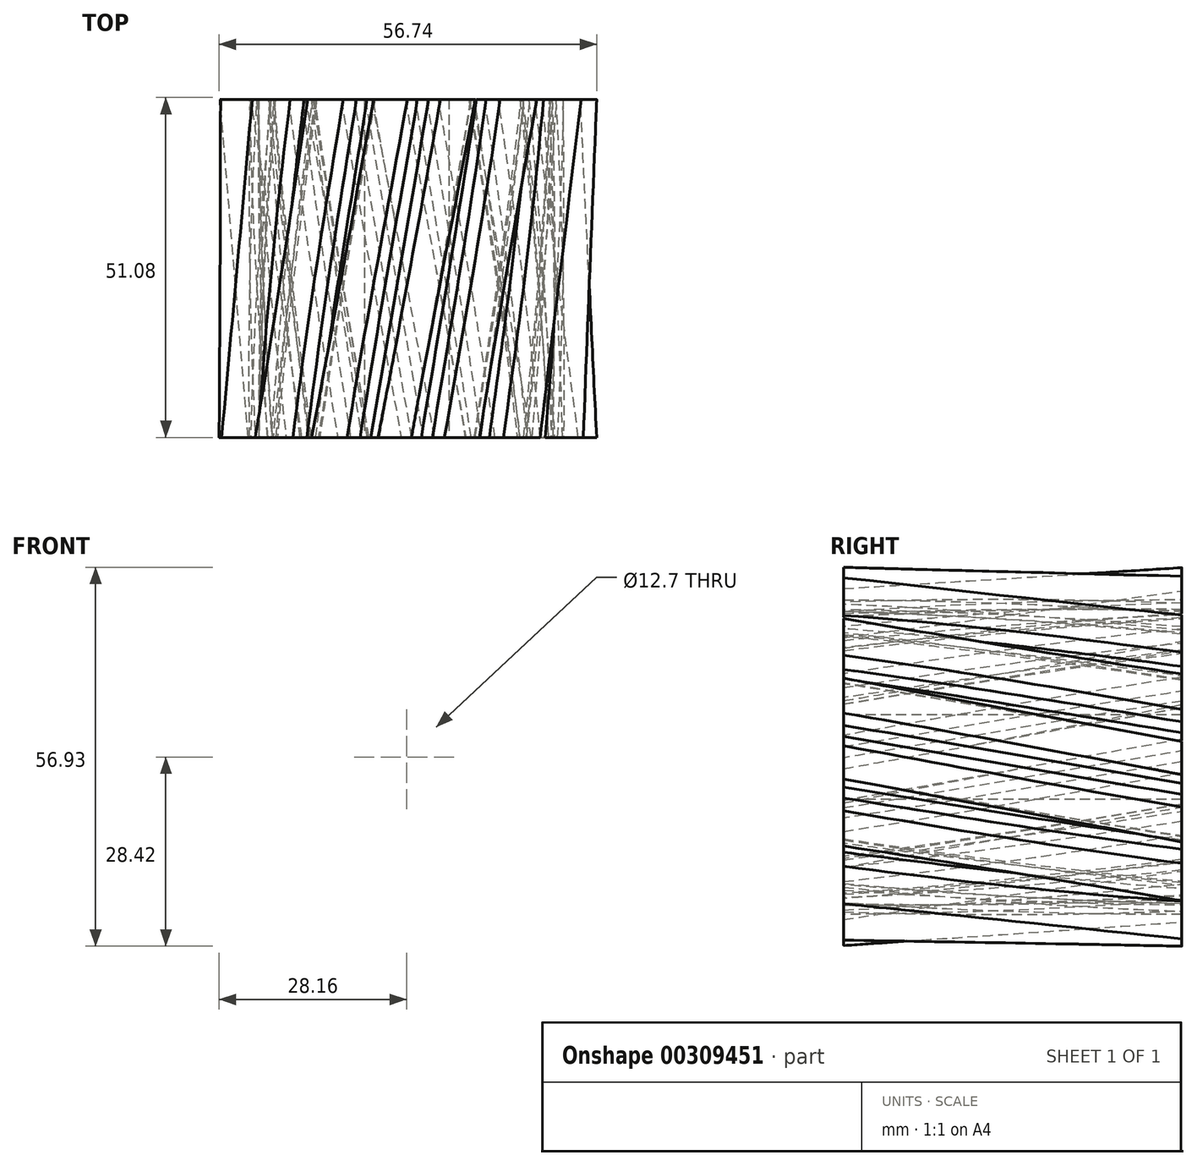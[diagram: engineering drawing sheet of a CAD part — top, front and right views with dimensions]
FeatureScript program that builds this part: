
annotation { "Feature Type Name" : "Feature", "Feature Type Description" : "" }
export const myFeature = defineFeature(function(context is Context, id is Id, definition is map)
    precondition{}
    {
        {
            var Q0;
            Q0=qCreatedBy(makeId("Front.planeOp"),FACE);
            var sketch = newSketch(context, id + "F0", { "sketchPlane" : qUnion([Q0])});
            skCircle(sketch, "E0", {"center": v(0, 0) * mm, "radius": 22.23 * mm});
            skArc(sketch, "E1.trimOffspring", {"start": v(-0.11, 25.67) * mm, "mid": v(-1.04, 27.17) * mm, "end": v(-2.34, 28.36) * mm});
            skLineSegment(sketch, "E2", {"start": v(0.02, 25.15) * mm, "end": v(0.23, 22.22) * mm});
            skLineSegment(sketch, "E3", {"start": v(-2.68, 28.45) * mm, "end": v(-2.8, 28.44) * mm});
            skLineSegment(sketch, "E4.MirrorCS", {"start": v(-2.93, 28.43) * mm, "end": v(-2.8, 28.44) * mm});
            skArc(sketch, "E5.MirrorCS", {"start": v(-4.9, 25.2) * mm, "mid": v(-4.28, 26.86) * mm, "end": v(-3.23, 28.28) * mm});
            skLineSegment(sketch, "E6.MirrorCS", {"start": v(-4.92, 24.66) * mm, "end": v(-4.56, 21.75) * mm});
            skPoint(sketch, "E7.visualSharp", {"position": v(0, 25.4) * mm});
            skArc(sketch, "E7.filletArc", {"start": v(0.02, 25.15) * mm, "mid": v(-0.02, 25.41) * mm, "end": v(-0.11, 25.67) * mm});
            skPoint(sketch, "E8.visualSharp", {"position": v(-4.96, 24.91) * mm});
            skArc(sketch, "E8.filletArc", {"start": v(-4.9, 25.2) * mm, "mid": v(-4.93, 24.93) * mm, "end": v(-4.92, 24.66) * mm});
            skPoint(sketch, "E9.visualSharp", {"position": v(-2.5, 28.47) * mm});
            skArc(sketch, "E9.filletArc", {"start": v(-2.34, 28.36) * mm, "mid": v(-2.5, 28.44) * mm, "end": v(-2.68, 28.45) * mm});
            skPoint(sketch, "E10.visualSharp", {"position": v(-3.1, 28.4) * mm});
            skArc(sketch, "E10.filletArc", {"start": v(-2.93, 28.43) * mm, "mid": v(-3.1, 28.38) * mm, "end": v(-3.23, 28.28) * mm});
            skSolve(sketch);
        }
        {
            var Q0;
            Q0=qCreatedBy(makeId("Front.planeOp"),FACE);
            cPlane(context, id + "F1", {"entities" : qUnion([Q0]), "cplaneType" : CPlaneType.OFFSET, "offset" : 50.8 * mm, "width" : 152.4 * mm, "height" : 152.4 * mm});
        }
        {
            var Q0;
            Q0=qCreatedBy(id+"F1.planeOp",FACE);
            var sketch = newSketch(context, id + "F2", { "sketchPlane" : qUnion([Q0])});
            skCircle(sketch, "E11.0", {"center": v(0, 0) * mm, "radius": 22.23 * mm});
            skArc(sketch, "E12.0.0", {"start": v(-3.23, 28.28) * mm, "mid": v(-4.28, 26.86) * mm, "end": v(-4.9, 25.2) * mm});
            skArc(sketch, "E12.0.1", {"start": v(-4.9, 25.2) * mm, "mid": v(-4.93, 24.93) * mm, "end": v(-4.92, 24.66) * mm});
            skLineSegment(sketch, "E12.0.2", {"start": v(-4.92, 24.66) * mm, "end": v(-4.56, 21.75) * mm});
            skArc(sketch, "E12.0.3", {"start": v(-4.56, 21.75) * mm, "mid": v(-2.18, 22.12) * mm, "end": v(0.23, 22.22) * mm});
            skLineSegment(sketch, "E12.0.4", {"start": v(0.23, 22.22) * mm, "end": v(0.02, 25.15) * mm});
            skArc(sketch, "E12.0.5", {"start": v(0.02, 25.15) * mm, "mid": v(-0.02, 25.41) * mm, "end": v(-0.11, 25.67) * mm});
            skArc(sketch, "E12.0.6", {"start": v(-0.11, 25.67) * mm, "mid": v(-1.04, 27.17) * mm, "end": v(-2.34, 28.36) * mm});
            skArc(sketch, "E12.0.7", {"start": v(-2.34, 28.36) * mm, "mid": v(-2.5, 28.44) * mm, "end": v(-2.68, 28.45) * mm});
            skLineSegment(sketch, "E12.0.8", {"start": v(-2.68, 28.45) * mm, "end": v(-2.8, 28.44) * mm});
            skLineSegment(sketch, "E12.0.9", {"start": v(-2.8, 28.44) * mm, "end": v(-2.93, 28.43) * mm});
            skArc(sketch, "E12.0.10", {"start": v(-2.93, 28.43) * mm, "mid": v(-3.1, 28.38) * mm, "end": v(-3.23, 28.28) * mm});
            skLineSegment(sketch, "E13.1.0", {"start": v(-13.99, 20.9) * mm, "end": v(-12.54, 18.35) * mm});
            skLineSegment(sketch, "E13.1.1", {"start": v(-13.47, 25.2) * mm, "end": v(-13.58, 25.14) * mm});
            skLineSegment(sketch, "E13.1.2", {"start": v(-13.36, 25.26) * mm, "end": v(-13.47, 25.2) * mm});
            skArc(sketch, "E13.1.3", {"start": v(-13.58, 25.14) * mm, "mid": v(-13.72, 25.03) * mm, "end": v(-13.8, 24.89) * mm});
            skArc(sketch, "E13.1.4", {"start": v(-13.02, 25.3) * mm, "mid": v(-13.2, 25.31) * mm, "end": v(-13.36, 25.26) * mm});
            skArc(sketch, "E13.1.5", {"start": v(-9.93, 23.68) * mm, "mid": v(-11.36, 24.7) * mm, "end": v(-13.02, 25.3) * mm});
            skArc(sketch, "E13.1.6", {"start": v(-13.8, 24.89) * mm, "mid": v(-14.23, 23.17) * mm, "end": v(-14.17, 21.4) * mm});
            skArc(sketch, "E13.1.7", {"start": v(-14.17, 21.4) * mm, "mid": v(-14.1, 21.15) * mm, "end": v(-13.99, 20.9) * mm});
            skArc(sketch, "E13.1.8", {"start": v(-9.6, 23.24) * mm, "mid": v(-9.75, 23.47) * mm, "end": v(-9.93, 23.68) * mm});
            skLineSegment(sketch, "E13.1.9", {"start": v(-8.3, 20.62) * mm, "end": v(-9.6, 23.24) * mm});
            skLineSegment(sketch, "E13.2.0", {"start": v(-20.92, 13.95) * mm, "end": v(-18.6, 12.15) * mm});
            skLineSegment(sketch, "E13.2.1", {"start": v(-22.1, 18.13) * mm, "end": v(-22.17, 18.03) * mm});
            skLineSegment(sketch, "E13.2.2", {"start": v(-22, 18.23) * mm, "end": v(-22.1, 18.13) * mm});
            skArc(sketch, "E13.2.3", {"start": v(-22.17, 18.03) * mm, "mid": v(-22.25, 17.88) * mm, "end": v(-22.28, 17.7) * mm});
            skArc(sketch, "E13.2.4", {"start": v(-21.71, 18.4) * mm, "mid": v(-21.88, 18.34) * mm, "end": v(-22, 18.23) * mm});
            skArc(sketch, "E13.2.5", {"start": v(-18.23, 18.07) * mm, "mid": v(-19.95, 18.48) * mm, "end": v(-21.71, 18.4) * mm});
            skArc(sketch, "E13.2.6", {"start": v(-22.28, 17.7) * mm, "mid": v(-22.02, 15.96) * mm, "end": v(-21.28, 14.36) * mm});
            skArc(sketch, "E13.2.7", {"start": v(-21.28, 14.36) * mm, "mid": v(-21.12, 14.14) * mm, "end": v(-20.92, 13.95) * mm});
            skArc(sketch, "E13.2.8", {"start": v(-17.77, 17.8) * mm, "mid": v(-17.99, 17.95) * mm, "end": v(-18.23, 18.07) * mm});
            skLineSegment(sketch, "E13.2.9", {"start": v(-15.55, 15.88) * mm, "end": v(-17.77, 17.8) * mm});
            skLineSegment(sketch, "E13.3.0", {"start": v(-24.67, 4.89) * mm, "end": v(-21.84, 4.1) * mm});
            skLineSegment(sketch, "E13.3.1", {"start": v(-27.35, 8.3) * mm, "end": v(-27.38, 8.17) * mm});
            skLineSegment(sketch, "E13.3.2", {"start": v(-27.3, 8.42) * mm, "end": v(-27.35, 8.3) * mm});
            skArc(sketch, "E13.3.3", {"start": v(-27.38, 8.17) * mm, "mid": v(-27.4, 8) * mm, "end": v(-27.36, 7.83) * mm});
            skArc(sketch, "E13.3.4", {"start": v(-27.1, 8.69) * mm, "mid": v(-27.23, 8.57) * mm, "end": v(-27.3, 8.42) * mm});
            skArc(sketch, "E13.3.5", {"start": v(-23.76, 9.72) * mm, "mid": v(-25.5, 9.44) * mm, "end": v(-27.1, 8.69) * mm});
            skArc(sketch, "E13.3.6", {"start": v(-27.36, 7.83) * mm, "mid": v(-26.45, 6.32) * mm, "end": v(-25.16, 5.12) * mm});
            skArc(sketch, "E13.3.7", {"start": v(-25.16, 5.12) * mm, "mid": v(-24.92, 4.98) * mm, "end": v(-24.67, 4.89) * mm});
            skArc(sketch, "E13.3.8", {"start": v(-23.22, 9.64) * mm, "mid": v(-23.49, 9.7) * mm, "end": v(-23.76, 9.72) * mm});
            skLineSegment(sketch, "E13.3.9", {"start": v(-20.44, 8.72) * mm, "end": v(-23.22, 9.64) * mm});
            skLineSegment(sketch, "E13.4.0", {"start": v(-24.66, -4.92) * mm, "end": v(-21.75, -4.56) * mm});
            skLineSegment(sketch, "E13.4.1", {"start": v(-28.44, -2.8) * mm, "end": v(-28.43, -2.93) * mm});
            skLineSegment(sketch, "E13.4.2", {"start": v(-28.45, -2.68) * mm, "end": v(-28.44, -2.8) * mm});
            skArc(sketch, "E13.4.3", {"start": v(-28.43, -2.93) * mm, "mid": v(-28.38, -3.1) * mm, "end": v(-28.28, -3.23) * mm});
            skArc(sketch, "E13.4.4", {"start": v(-28.36, -2.34) * mm, "mid": v(-28.44, -2.5) * mm, "end": v(-28.45, -2.68) * mm});
            skArc(sketch, "E13.4.5", {"start": v(-25.67, -0.11) * mm, "mid": v(-27.17, -1.04) * mm, "end": v(-28.36, -2.34) * mm});
            skArc(sketch, "E13.4.6", {"start": v(-28.28, -3.23) * mm, "mid": v(-26.86, -4.28) * mm, "end": v(-25.2, -4.9) * mm});
            skArc(sketch, "E13.4.7", {"start": v(-25.2, -4.9) * mm, "mid": v(-24.93, -4.93) * mm, "end": v(-24.66, -4.92) * mm});
            skArc(sketch, "E13.4.8", {"start": v(-25.15, 0.02) * mm, "mid": v(-25.41, -0.02) * mm, "end": v(-25.67, -0.11) * mm});
            skLineSegment(sketch, "E13.4.9", {"start": v(-22.22, 0.23) * mm, "end": v(-25.15, 0.02) * mm});
            skLineSegment(sketch, "E13.5.0", {"start": v(-20.9, -13.99) * mm, "end": v(-18.35, -12.54) * mm});
            skLineSegment(sketch, "E13.5.1", {"start": v(-25.2, -13.47) * mm, "end": v(-25.14, -13.58) * mm});
            skLineSegment(sketch, "E13.5.2", {"start": v(-25.26, -13.36) * mm, "end": v(-25.2, -13.47) * mm});
            skArc(sketch, "E13.5.3", {"start": v(-25.14, -13.58) * mm, "mid": v(-25.03, -13.72) * mm, "end": v(-24.89, -13.8) * mm});
            skArc(sketch, "E13.5.4", {"start": v(-25.3, -13.02) * mm, "mid": v(-25.31, -13.2) * mm, "end": v(-25.26, -13.36) * mm});
            skArc(sketch, "E13.5.5", {"start": v(-23.68, -9.93) * mm, "mid": v(-24.7, -11.36) * mm, "end": v(-25.3, -13.02) * mm});
            skArc(sketch, "E13.5.6", {"start": v(-24.89, -13.8) * mm, "mid": v(-23.17, -14.23) * mm, "end": v(-21.4, -14.17) * mm});
            skArc(sketch, "E13.5.7", {"start": v(-21.4, -14.17) * mm, "mid": v(-21.15, -14.1) * mm, "end": v(-20.9, -13.99) * mm});
            skArc(sketch, "E13.5.8", {"start": v(-23.24, -9.6) * mm, "mid": v(-23.47, -9.75) * mm, "end": v(-23.68, -9.93) * mm});
            skLineSegment(sketch, "E13.5.9", {"start": v(-20.62, -8.3) * mm, "end": v(-23.24, -9.6) * mm});
            skLineSegment(sketch, "E13.6.0", {"start": v(-13.95, -20.92) * mm, "end": v(-12.15, -18.6) * mm});
            skLineSegment(sketch, "E13.6.1", {"start": v(-18.13, -22.1) * mm, "end": v(-18.03, -22.17) * mm});
            skLineSegment(sketch, "E13.6.2", {"start": v(-18.23, -22) * mm, "end": v(-18.13, -22.1) * mm});
            skArc(sketch, "E13.6.3", {"start": v(-18.03, -22.17) * mm, "mid": v(-17.88, -22.25) * mm, "end": v(-17.7, -22.28) * mm});
            skArc(sketch, "E13.6.4", {"start": v(-18.4, -21.71) * mm, "mid": v(-18.34, -21.88) * mm, "end": v(-18.23, -22) * mm});
            skArc(sketch, "E13.6.5", {"start": v(-18.07, -18.23) * mm, "mid": v(-18.48, -19.95) * mm, "end": v(-18.4, -21.71) * mm});
            skArc(sketch, "E13.6.6", {"start": v(-17.7, -22.28) * mm, "mid": v(-15.96, -22.02) * mm, "end": v(-14.36, -21.28) * mm});
            skArc(sketch, "E13.6.7", {"start": v(-14.36, -21.28) * mm, "mid": v(-14.14, -21.12) * mm, "end": v(-13.95, -20.92) * mm});
            skArc(sketch, "E13.6.8", {"start": v(-17.8, -17.77) * mm, "mid": v(-17.95, -17.99) * mm, "end": v(-18.07, -18.23) * mm});
            skLineSegment(sketch, "E13.6.9", {"start": v(-15.88, -15.55) * mm, "end": v(-17.8, -17.77) * mm});
            skLineSegment(sketch, "E13.7.0", {"start": v(-4.89, -24.67) * mm, "end": v(-4.1, -21.84) * mm});
            skLineSegment(sketch, "E13.7.1", {"start": v(-8.3, -27.35) * mm, "end": v(-8.17, -27.38) * mm});
            skLineSegment(sketch, "E13.7.2", {"start": v(-8.42, -27.3) * mm, "end": v(-8.3, -27.35) * mm});
            skArc(sketch, "E13.7.3", {"start": v(-8.17, -27.38) * mm, "mid": v(-8, -27.4) * mm, "end": v(-7.83, -27.36) * mm});
            skArc(sketch, "E13.7.4", {"start": v(-8.69, -27.1) * mm, "mid": v(-8.57, -27.23) * mm, "end": v(-8.42, -27.3) * mm});
            skArc(sketch, "E13.7.5", {"start": v(-9.72, -23.76) * mm, "mid": v(-9.44, -25.5) * mm, "end": v(-8.69, -27.1) * mm});
            skArc(sketch, "E13.7.6", {"start": v(-7.83, -27.36) * mm, "mid": v(-6.32, -26.45) * mm, "end": v(-5.12, -25.16) * mm});
            skArc(sketch, "E13.7.7", {"start": v(-5.12, -25.16) * mm, "mid": v(-4.98, -24.92) * mm, "end": v(-4.89, -24.67) * mm});
            skArc(sketch, "E13.7.8", {"start": v(-9.64, -23.22) * mm, "mid": v(-9.7, -23.49) * mm, "end": v(-9.72, -23.76) * mm});
            skLineSegment(sketch, "E13.7.9", {"start": v(-8.72, -20.44) * mm, "end": v(-9.64, -23.22) * mm});
            skLineSegment(sketch, "E13.8.0", {"start": v(4.92, -24.66) * mm, "end": v(4.56, -21.75) * mm});
            skLineSegment(sketch, "E13.8.1", {"start": v(2.8, -28.44) * mm, "end": v(2.93, -28.43) * mm});
            skLineSegment(sketch, "E13.8.2", {"start": v(2.68, -28.45) * mm, "end": v(2.8, -28.44) * mm});
            skArc(sketch, "E13.8.3", {"start": v(2.93, -28.43) * mm, "mid": v(3.1, -28.38) * mm, "end": v(3.23, -28.28) * mm});
            skArc(sketch, "E13.8.4", {"start": v(2.34, -28.36) * mm, "mid": v(2.5, -28.44) * mm, "end": v(2.68, -28.45) * mm});
            skArc(sketch, "E13.8.5", {"start": v(0.11, -25.67) * mm, "mid": v(1.04, -27.17) * mm, "end": v(2.34, -28.36) * mm});
            skArc(sketch, "E13.8.6", {"start": v(3.23, -28.28) * mm, "mid": v(4.28, -26.86) * mm, "end": v(4.9, -25.2) * mm});
            skArc(sketch, "E13.8.7", {"start": v(4.9, -25.2) * mm, "mid": v(4.93, -24.93) * mm, "end": v(4.92, -24.66) * mm});
            skArc(sketch, "E13.8.8", {"start": v(-0.02, -25.15) * mm, "mid": v(0.02, -25.41) * mm, "end": v(0.11, -25.67) * mm});
            skLineSegment(sketch, "E13.8.9", {"start": v(-0.23, -22.22) * mm, "end": v(-0.02, -25.15) * mm});
            skLineSegment(sketch, "E13.9.0", {"start": v(13.99, -20.9) * mm, "end": v(12.54, -18.35) * mm});
            skLineSegment(sketch, "E13.9.1", {"start": v(13.47, -25.2) * mm, "end": v(13.58, -25.14) * mm});
            skLineSegment(sketch, "E13.9.2", {"start": v(13.36, -25.26) * mm, "end": v(13.47, -25.2) * mm});
            skArc(sketch, "E13.9.3", {"start": v(13.58, -25.14) * mm, "mid": v(13.72, -25.03) * mm, "end": v(13.8, -24.89) * mm});
            skArc(sketch, "E13.9.4", {"start": v(13.02, -25.3) * mm, "mid": v(13.2, -25.31) * mm, "end": v(13.36, -25.26) * mm});
            skArc(sketch, "E13.9.5", {"start": v(9.93, -23.68) * mm, "mid": v(11.36, -24.7) * mm, "end": v(13.02, -25.3) * mm});
            skArc(sketch, "E13.9.6", {"start": v(13.8, -24.89) * mm, "mid": v(14.23, -23.17) * mm, "end": v(14.17, -21.4) * mm});
            skArc(sketch, "E13.9.7", {"start": v(14.17, -21.4) * mm, "mid": v(14.1, -21.15) * mm, "end": v(13.99, -20.9) * mm});
            skArc(sketch, "E13.9.8", {"start": v(9.6, -23.24) * mm, "mid": v(9.75, -23.47) * mm, "end": v(9.93, -23.68) * mm});
            skLineSegment(sketch, "E13.9.9", {"start": v(8.3, -20.62) * mm, "end": v(9.6, -23.24) * mm});
            skLineSegment(sketch, "E13.10.0", {"start": v(20.92, -13.95) * mm, "end": v(18.6, -12.15) * mm});
            skLineSegment(sketch, "E13.10.1", {"start": v(22.1, -18.13) * mm, "end": v(22.17, -18.03) * mm});
            skLineSegment(sketch, "E13.10.2", {"start": v(22, -18.23) * mm, "end": v(22.1, -18.13) * mm});
            skArc(sketch, "E13.10.3", {"start": v(22.17, -18.03) * mm, "mid": v(22.25, -17.88) * mm, "end": v(22.28, -17.7) * mm});
            skArc(sketch, "E13.10.4", {"start": v(21.71, -18.4) * mm, "mid": v(21.88, -18.34) * mm, "end": v(22, -18.23) * mm});
            skArc(sketch, "E13.10.5", {"start": v(18.23, -18.07) * mm, "mid": v(19.95, -18.48) * mm, "end": v(21.71, -18.4) * mm});
            skArc(sketch, "E13.10.6", {"start": v(22.28, -17.7) * mm, "mid": v(22.02, -15.96) * mm, "end": v(21.28, -14.36) * mm});
            skArc(sketch, "E13.10.7", {"start": v(21.28, -14.36) * mm, "mid": v(21.12, -14.14) * mm, "end": v(20.92, -13.95) * mm});
            skArc(sketch, "E13.10.8", {"start": v(17.77, -17.8) * mm, "mid": v(17.99, -17.95) * mm, "end": v(18.23, -18.07) * mm});
            skLineSegment(sketch, "E13.10.9", {"start": v(15.55, -15.88) * mm, "end": v(17.77, -17.8) * mm});
            skLineSegment(sketch, "E13.11.0", {"start": v(24.67, -4.89) * mm, "end": v(21.84, -4.1) * mm});
            skLineSegment(sketch, "E13.11.1", {"start": v(27.35, -8.3) * mm, "end": v(27.38, -8.17) * mm});
            skLineSegment(sketch, "E13.11.2", {"start": v(27.3, -8.42) * mm, "end": v(27.35, -8.3) * mm});
            skArc(sketch, "E13.11.3", {"start": v(27.38, -8.17) * mm, "mid": v(27.4, -8) * mm, "end": v(27.36, -7.83) * mm});
            skArc(sketch, "E13.11.4", {"start": v(27.1, -8.69) * mm, "mid": v(27.23, -8.57) * mm, "end": v(27.3, -8.42) * mm});
            skArc(sketch, "E13.11.5", {"start": v(23.76, -9.72) * mm, "mid": v(25.5, -9.44) * mm, "end": v(27.1, -8.69) * mm});
            skArc(sketch, "E13.11.6", {"start": v(27.36, -7.83) * mm, "mid": v(26.45, -6.32) * mm, "end": v(25.16, -5.12) * mm});
            skArc(sketch, "E13.11.7", {"start": v(25.16, -5.12) * mm, "mid": v(24.92, -4.98) * mm, "end": v(24.67, -4.89) * mm});
            skArc(sketch, "E13.11.8", {"start": v(23.22, -9.64) * mm, "mid": v(23.49, -9.7) * mm, "end": v(23.76, -9.72) * mm});
            skLineSegment(sketch, "E13.11.9", {"start": v(20.44, -8.72) * mm, "end": v(23.22, -9.64) * mm});
            skLineSegment(sketch, "E13.12.0", {"start": v(24.66, 4.92) * mm, "end": v(21.75, 4.56) * mm});
            skLineSegment(sketch, "E13.12.1", {"start": v(28.44, 2.8) * mm, "end": v(28.43, 2.93) * mm});
            skLineSegment(sketch, "E13.12.2", {"start": v(28.45, 2.68) * mm, "end": v(28.44, 2.8) * mm});
            skArc(sketch, "E13.12.3", {"start": v(28.43, 2.93) * mm, "mid": v(28.38, 3.1) * mm, "end": v(28.28, 3.23) * mm});
            skArc(sketch, "E13.12.4", {"start": v(28.36, 2.34) * mm, "mid": v(28.44, 2.5) * mm, "end": v(28.45, 2.68) * mm});
            skArc(sketch, "E13.12.5", {"start": v(25.67, 0.11) * mm, "mid": v(27.17, 1.04) * mm, "end": v(28.36, 2.34) * mm});
            skArc(sketch, "E13.12.6", {"start": v(28.28, 3.23) * mm, "mid": v(26.86, 4.28) * mm, "end": v(25.2, 4.9) * mm});
            skArc(sketch, "E13.12.7", {"start": v(25.2, 4.9) * mm, "mid": v(24.93, 4.93) * mm, "end": v(24.66, 4.92) * mm});
            skArc(sketch, "E13.12.8", {"start": v(25.15, -0.02) * mm, "mid": v(25.41, 0.02) * mm, "end": v(25.67, 0.11) * mm});
            skLineSegment(sketch, "E13.12.9", {"start": v(22.22, -0.23) * mm, "end": v(25.15, -0.02) * mm});
            skLineSegment(sketch, "E13.13.0", {"start": v(20.9, 13.99) * mm, "end": v(18.35, 12.54) * mm});
            skLineSegment(sketch, "E13.13.1", {"start": v(25.2, 13.47) * mm, "end": v(25.14, 13.58) * mm});
            skLineSegment(sketch, "E13.13.2", {"start": v(25.26, 13.36) * mm, "end": v(25.2, 13.47) * mm});
            skArc(sketch, "E13.13.3", {"start": v(25.14, 13.58) * mm, "mid": v(25.03, 13.72) * mm, "end": v(24.89, 13.8) * mm});
            skArc(sketch, "E13.13.4", {"start": v(25.3, 13.02) * mm, "mid": v(25.31, 13.2) * mm, "end": v(25.26, 13.36) * mm});
            skArc(sketch, "E13.13.5", {"start": v(23.68, 9.93) * mm, "mid": v(24.7, 11.36) * mm, "end": v(25.3, 13.02) * mm});
            skArc(sketch, "E13.13.6", {"start": v(24.89, 13.8) * mm, "mid": v(23.17, 14.23) * mm, "end": v(21.4, 14.17) * mm});
            skArc(sketch, "E13.13.7", {"start": v(21.4, 14.17) * mm, "mid": v(21.15, 14.1) * mm, "end": v(20.9, 13.99) * mm});
            skArc(sketch, "E13.13.8", {"start": v(23.24, 9.6) * mm, "mid": v(23.47, 9.75) * mm, "end": v(23.68, 9.93) * mm});
            skLineSegment(sketch, "E13.13.9", {"start": v(20.62, 8.3) * mm, "end": v(23.24, 9.6) * mm});
            skLineSegment(sketch, "E13.14.0", {"start": v(13.95, 20.92) * mm, "end": v(12.15, 18.6) * mm});
            skLineSegment(sketch, "E13.14.1", {"start": v(18.13, 22.1) * mm, "end": v(18.03, 22.17) * mm});
            skLineSegment(sketch, "E13.14.2", {"start": v(18.23, 22) * mm, "end": v(18.13, 22.1) * mm});
            skArc(sketch, "E13.14.3", {"start": v(18.03, 22.17) * mm, "mid": v(17.88, 22.25) * mm, "end": v(17.7, 22.28) * mm});
            skArc(sketch, "E13.14.4", {"start": v(18.4, 21.71) * mm, "mid": v(18.34, 21.88) * mm, "end": v(18.23, 22) * mm});
            skArc(sketch, "E13.14.5", {"start": v(18.07, 18.23) * mm, "mid": v(18.48, 19.95) * mm, "end": v(18.4, 21.71) * mm});
            skArc(sketch, "E13.14.6", {"start": v(17.7, 22.28) * mm, "mid": v(15.96, 22.02) * mm, "end": v(14.36, 21.28) * mm});
            skArc(sketch, "E13.14.7", {"start": v(14.36, 21.28) * mm, "mid": v(14.14, 21.12) * mm, "end": v(13.95, 20.92) * mm});
            skArc(sketch, "E13.14.8", {"start": v(17.8, 17.77) * mm, "mid": v(17.95, 17.99) * mm, "end": v(18.07, 18.23) * mm});
            skLineSegment(sketch, "E13.14.9", {"start": v(15.88, 15.55) * mm, "end": v(17.8, 17.77) * mm});
            skLineSegment(sketch, "E13.15.0", {"start": v(4.89, 24.67) * mm, "end": v(4.1, 21.84) * mm});
            skLineSegment(sketch, "E13.15.1", {"start": v(8.3, 27.35) * mm, "end": v(8.17, 27.38) * mm});
            skLineSegment(sketch, "E13.15.2", {"start": v(8.42, 27.3) * mm, "end": v(8.3, 27.35) * mm});
            skArc(sketch, "E13.15.3", {"start": v(8.17, 27.38) * mm, "mid": v(8, 27.4) * mm, "end": v(7.83, 27.36) * mm});
            skArc(sketch, "E13.15.4", {"start": v(8.69, 27.1) * mm, "mid": v(8.57, 27.23) * mm, "end": v(8.42, 27.3) * mm});
            skArc(sketch, "E13.15.5", {"start": v(9.72, 23.76) * mm, "mid": v(9.44, 25.5) * mm, "end": v(8.69, 27.1) * mm});
            skArc(sketch, "E13.15.6", {"start": v(7.83, 27.36) * mm, "mid": v(6.32, 26.45) * mm, "end": v(5.12, 25.16) * mm});
            skArc(sketch, "E13.15.7", {"start": v(5.12, 25.16) * mm, "mid": v(4.98, 24.92) * mm, "end": v(4.89, 24.67) * mm});
            skArc(sketch, "E13.15.8", {"start": v(9.64, 23.22) * mm, "mid": v(9.7, 23.49) * mm, "end": v(9.72, 23.76) * mm});
            skLineSegment(sketch, "E13.15.9", {"start": v(8.72, 20.44) * mm, "end": v(9.64, 23.22) * mm});
            skSolve(sketch);
        }
        {
            var Q0;
            Q0=makeQuery(id+"F0.imprint","IMPRINT",FACE,{"disambiguationData":[TD([[makeQuery(id+"F0.imprint","IMPRINT",EDGE,{"derivedFrom":sQuery(id+"F0.wireOp",EDGE,"E1.trimOffspring")}),1.0]])]});
            var Q1;
            {var subQ0=sQuery(id+"F2.wireOp",EDGE,"E13.1.0");Q1=makeQuery(id+"F2.imprint","IMPRINT",FACE,{"disambiguationData":[TD([[makeQuery(id+"F2.imprint","IMPRINT",EDGE,{"derivedFrom":subQ0}),1.0]])]});}
            loft(context, id + "F3", {"sheetProfilesArray" : [{ "sheetProfileEntities" : qUnion([Q0]) }, { "sheetProfileEntities" : qUnion([Q1]) }]});
        }
        {
            var Q0;
            Q0=qCreatedBy(id+"F1.planeOp",FACE);
            var sketch = newSketch(context, id + "F4", { "sketchPlane" : qUnion([Q0])});
            skCircle(sketch, "E14", {"center": v(0, 0) * mm, "radius": 22.23 * mm});
            skSolve(sketch);
        }
        {
            var Q0;
            Q0 = qSketchRegion(id + "F4", true);
            extrude(context, id + "F5", {"entities" : qUnion([Q0]), "operationType" : NewBodyOperationType.ADD, "oppositeDirection" : true, "depth" : 50.8 * mm});
        }
        {
            var Q0;
            {var subQ0=sQuery(id+"F2.wireOp",EDGE,"E13.1.0");Q0=makeQuery(id+"F3.opLoft","SWEPT_BODY",BODY,{"disambiguationData":[OSD([makeQuery(id+"F0.imprint","IMPRINT",FACE,{"disambiguationData":[TD([[makeQuery(id+"F0.imprint","IMPRINT",EDGE,{"derivedFrom":sQuery(id+"F0.wireOp",EDGE,"E1.trimOffspring")}),1.0]])]}),makeQuery(id+"F2.imprint","IMPRINT",FACE,{"disambiguationData":[TD([[makeQuery(id+"F2.imprint","IMPRINT",EDGE,{"derivedFrom":subQ0}),1.0]])]})])]});}
            var Q1;
            Q1=makeQuery(id+"F5.opExtrude","SWEPT_FACE",FACE,{"disambiguationData":[OSD([sQuery(id+"F4.wireOp",EDGE,"E14")])]});
            circularPattern(context, id + "F6", {"entities" : qUnion([Q0]), "axis" : qUnion([Q1]), "angle" : 360 * degree, "instanceCount" : 15, "equalSpace" : true});
        }
        {
            var Q0;
            Q0=makeQuery(id+"F6.opPattern","COPY",EDGE,{"derivedFrom":makeQuery(id+"F5.boolean.opBoolean","INTERSECT",EDGE,{"derivedFrom":[makeQuery(id+"F3.opLoft","SWEPT_FACE",FACE,{"disambiguationData":[OSD([sQuery(id+"F0.wireOp",EDGE,"E0"),sQuery(id+"F0.wireOp",EDGE,"E2"),sQuery(id+"F0.wireOp",EDGE,"E7.filletArc"),sQuery(id+"F2.wireOp",EDGE,"E11.0"),sQuery(id+"F2.wireOp",EDGE,"E13.1.8"),sQuery(id+"F2.wireOp",EDGE,"E13.1.9")])]}),makeQuery(id+"F5.opExtrude","SWEPT_FACE",FACE,{"disambiguationData":[OSD([sQuery(id+"F4.wireOp",EDGE,"E14")])]})]}),"instanceName":"13"});
            var Q1;
            Q1=makeQuery(id+"F6.opPattern","COPY",EDGE,{"derivedFrom":makeQuery(id+"F5.boolean.opBoolean","INTERSECT",EDGE,{"derivedFrom":[makeQuery(id+"F3.opLoft","SWEPT_FACE",FACE,{"disambiguationData":[OSD([sQuery(id+"F0.wireOp",EDGE,"E0"),sQuery(id+"F0.wireOp",EDGE,"E2"),sQuery(id+"F0.wireOp",EDGE,"E7.filletArc"),sQuery(id+"F2.wireOp",EDGE,"E11.0"),sQuery(id+"F2.wireOp",EDGE,"E13.1.8"),sQuery(id+"F2.wireOp",EDGE,"E13.1.9")])]}),makeQuery(id+"F5.opExtrude","SWEPT_FACE",FACE,{"disambiguationData":[OSD([sQuery(id+"F4.wireOp",EDGE,"E14")])]})]}),"instanceName":"14"});
            var Q2;
            Q2=makeQuery(id+"F5.boolean.opBoolean","INTERSECT",EDGE,{"derivedFrom":[makeQuery(id+"F3.opLoft","SWEPT_FACE",FACE,{"disambiguationData":[OSD([sQuery(id+"F0.wireOp",EDGE,"E0"),sQuery(id+"F0.wireOp",EDGE,"E2"),sQuery(id+"F0.wireOp",EDGE,"E7.filletArc"),sQuery(id+"F2.wireOp",EDGE,"E11.0"),sQuery(id+"F2.wireOp",EDGE,"E13.1.8"),sQuery(id+"F2.wireOp",EDGE,"E13.1.9")])]}),makeQuery(id+"F5.opExtrude","SWEPT_FACE",FACE,{"disambiguationData":[OSD([sQuery(id+"F4.wireOp",EDGE,"E14")])]})]});
            var Q3;
            Q3=makeQuery(id+"F6.opPattern","COPY",EDGE,{"derivedFrom":makeQuery(id+"F5.boolean.opBoolean","INTERSECT",EDGE,{"derivedFrom":[makeQuery(id+"F3.opLoft","SWEPT_FACE",FACE,{"disambiguationData":[OSD([sQuery(id+"F0.wireOp",EDGE,"E0"),sQuery(id+"F0.wireOp",EDGE,"E2"),sQuery(id+"F0.wireOp",EDGE,"E7.filletArc"),sQuery(id+"F2.wireOp",EDGE,"E11.0"),sQuery(id+"F2.wireOp",EDGE,"E13.1.8"),sQuery(id+"F2.wireOp",EDGE,"E13.1.9")])]}),makeQuery(id+"F5.opExtrude","SWEPT_FACE",FACE,{"disambiguationData":[OSD([sQuery(id+"F4.wireOp",EDGE,"E14")])]})]}),"instanceName":"1"});
            var Q4;
            Q4=makeQuery(id+"F6.opPattern","COPY",EDGE,{"derivedFrom":makeQuery(id+"F5.boolean.opBoolean","INTERSECT",EDGE,{"derivedFrom":[makeQuery(id+"F3.opLoft","SWEPT_FACE",FACE,{"disambiguationData":[OSD([sQuery(id+"F0.wireOp",EDGE,"E0"),sQuery(id+"F0.wireOp",EDGE,"E2"),sQuery(id+"F0.wireOp",EDGE,"E7.filletArc"),sQuery(id+"F2.wireOp",EDGE,"E11.0"),sQuery(id+"F2.wireOp",EDGE,"E13.1.8"),sQuery(id+"F2.wireOp",EDGE,"E13.1.9")])]}),makeQuery(id+"F5.opExtrude","SWEPT_FACE",FACE,{"disambiguationData":[OSD([sQuery(id+"F4.wireOp",EDGE,"E14")])]})]}),"instanceName":"2"});
            var Q5;
            Q5=makeQuery(id+"F6.opPattern","COPY",EDGE,{"derivedFrom":makeQuery(id+"F5.boolean.opBoolean","INTERSECT",EDGE,{"derivedFrom":[makeQuery(id+"F3.opLoft","SWEPT_FACE",FACE,{"disambiguationData":[OSD([sQuery(id+"F0.wireOp",EDGE,"E0"),sQuery(id+"F0.wireOp",EDGE,"E2"),sQuery(id+"F0.wireOp",EDGE,"E7.filletArc"),sQuery(id+"F2.wireOp",EDGE,"E11.0"),sQuery(id+"F2.wireOp",EDGE,"E13.1.8"),sQuery(id+"F2.wireOp",EDGE,"E13.1.9")])]}),makeQuery(id+"F5.opExtrude","SWEPT_FACE",FACE,{"disambiguationData":[OSD([sQuery(id+"F4.wireOp",EDGE,"E14")])]})]}),"instanceName":"3"});
            var Q6;
            Q6=makeQuery(id+"F6.opPattern","COPY",EDGE,{"derivedFrom":makeQuery(id+"F5.boolean.opBoolean","INTERSECT",EDGE,{"derivedFrom":[makeQuery(id+"F3.opLoft","SWEPT_FACE",FACE,{"disambiguationData":[OSD([sQuery(id+"F0.wireOp",EDGE,"E0"),sQuery(id+"F0.wireOp",EDGE,"E2"),sQuery(id+"F0.wireOp",EDGE,"E7.filletArc"),sQuery(id+"F2.wireOp",EDGE,"E11.0"),sQuery(id+"F2.wireOp",EDGE,"E13.1.8"),sQuery(id+"F2.wireOp",EDGE,"E13.1.9")])]}),makeQuery(id+"F5.opExtrude","SWEPT_FACE",FACE,{"disambiguationData":[OSD([sQuery(id+"F4.wireOp",EDGE,"E14")])]})]}),"instanceName":"4"});
            var Q7;
            Q7=makeQuery(id+"F6.opPattern","COPY",EDGE,{"derivedFrom":makeQuery(id+"F5.boolean.opBoolean","INTERSECT",EDGE,{"derivedFrom":[makeQuery(id+"F3.opLoft","SWEPT_FACE",FACE,{"disambiguationData":[OSD([sQuery(id+"F0.wireOp",EDGE,"E0"),sQuery(id+"F0.wireOp",EDGE,"E2"),sQuery(id+"F0.wireOp",EDGE,"E7.filletArc"),sQuery(id+"F2.wireOp",EDGE,"E11.0"),sQuery(id+"F2.wireOp",EDGE,"E13.1.8"),sQuery(id+"F2.wireOp",EDGE,"E13.1.9")])]}),makeQuery(id+"F5.opExtrude","SWEPT_FACE",FACE,{"disambiguationData":[OSD([sQuery(id+"F4.wireOp",EDGE,"E14")])]})]}),"instanceName":"6"});
            var Q8;
            Q8=makeQuery(id+"F6.opPattern","COPY",EDGE,{"derivedFrom":makeQuery(id+"F5.boolean.opBoolean","INTERSECT",EDGE,{"derivedFrom":[makeQuery(id+"F3.opLoft","SWEPT_FACE",FACE,{"disambiguationData":[OSD([sQuery(id+"F0.wireOp",EDGE,"E0"),sQuery(id+"F0.wireOp",EDGE,"E2"),sQuery(id+"F0.wireOp",EDGE,"E7.filletArc"),sQuery(id+"F2.wireOp",EDGE,"E11.0"),sQuery(id+"F2.wireOp",EDGE,"E13.1.8"),sQuery(id+"F2.wireOp",EDGE,"E13.1.9")])]}),makeQuery(id+"F5.opExtrude","SWEPT_FACE",FACE,{"disambiguationData":[OSD([sQuery(id+"F4.wireOp",EDGE,"E14")])]})]}),"instanceName":"5"});
            var Q9;
            Q9=makeQuery(id+"F6.opPattern","COPY",EDGE,{"derivedFrom":makeQuery(id+"F5.boolean.opBoolean","INTERSECT",EDGE,{"derivedFrom":[makeQuery(id+"F3.opLoft","SWEPT_FACE",FACE,{"disambiguationData":[OSD([sQuery(id+"F0.wireOp",EDGE,"E0"),sQuery(id+"F0.wireOp",EDGE,"E2"),sQuery(id+"F0.wireOp",EDGE,"E7.filletArc"),sQuery(id+"F2.wireOp",EDGE,"E11.0"),sQuery(id+"F2.wireOp",EDGE,"E13.1.8"),sQuery(id+"F2.wireOp",EDGE,"E13.1.9")])]}),makeQuery(id+"F5.opExtrude","SWEPT_FACE",FACE,{"disambiguationData":[OSD([sQuery(id+"F4.wireOp",EDGE,"E14")])]})]}),"instanceName":"7"});
            var Q10;
            Q10=makeQuery(id+"F6.opPattern","COPY",EDGE,{"derivedFrom":makeQuery(id+"F5.boolean.opBoolean","INTERSECT",EDGE,{"derivedFrom":[makeQuery(id+"F3.opLoft","SWEPT_FACE",FACE,{"disambiguationData":[OSD([sQuery(id+"F0.wireOp",EDGE,"E0"),sQuery(id+"F0.wireOp",EDGE,"E2"),sQuery(id+"F0.wireOp",EDGE,"E7.filletArc"),sQuery(id+"F2.wireOp",EDGE,"E11.0"),sQuery(id+"F2.wireOp",EDGE,"E13.1.8"),sQuery(id+"F2.wireOp",EDGE,"E13.1.9")])]}),makeQuery(id+"F5.opExtrude","SWEPT_FACE",FACE,{"disambiguationData":[OSD([sQuery(id+"F4.wireOp",EDGE,"E14")])]})]}),"instanceName":"8"});
            var Q11;
            Q11=makeQuery(id+"F6.opPattern","COPY",EDGE,{"derivedFrom":makeQuery(id+"F5.boolean.opBoolean","INTERSECT",EDGE,{"derivedFrom":[makeQuery(id+"F3.opLoft","SWEPT_FACE",FACE,{"disambiguationData":[OSD([sQuery(id+"F0.wireOp",EDGE,"E0"),sQuery(id+"F0.wireOp",EDGE,"E2"),sQuery(id+"F0.wireOp",EDGE,"E7.filletArc"),sQuery(id+"F2.wireOp",EDGE,"E11.0"),sQuery(id+"F2.wireOp",EDGE,"E13.1.8"),sQuery(id+"F2.wireOp",EDGE,"E13.1.9")])]}),makeQuery(id+"F5.opExtrude","SWEPT_FACE",FACE,{"disambiguationData":[OSD([sQuery(id+"F4.wireOp",EDGE,"E14")])]})]}),"instanceName":"9"});
            var Q12;
            Q12=makeQuery(id+"F6.opPattern","COPY",EDGE,{"derivedFrom":makeQuery(id+"F5.boolean.opBoolean","INTERSECT",EDGE,{"derivedFrom":[makeQuery(id+"F3.opLoft","SWEPT_FACE",FACE,{"disambiguationData":[OSD([sQuery(id+"F0.wireOp",EDGE,"E0"),sQuery(id+"F0.wireOp",EDGE,"E2"),sQuery(id+"F0.wireOp",EDGE,"E7.filletArc"),sQuery(id+"F2.wireOp",EDGE,"E11.0"),sQuery(id+"F2.wireOp",EDGE,"E13.1.8"),sQuery(id+"F2.wireOp",EDGE,"E13.1.9")])]}),makeQuery(id+"F5.opExtrude","SWEPT_FACE",FACE,{"disambiguationData":[OSD([sQuery(id+"F4.wireOp",EDGE,"E14")])]})]}),"instanceName":"10"});
            var Q13;
            Q13=makeQuery(id+"F6.opPattern","COPY",EDGE,{"derivedFrom":makeQuery(id+"F5.boolean.opBoolean","INTERSECT",EDGE,{"derivedFrom":[makeQuery(id+"F3.opLoft","SWEPT_FACE",FACE,{"disambiguationData":[OSD([sQuery(id+"F0.wireOp",EDGE,"E0"),sQuery(id+"F0.wireOp",EDGE,"E2"),sQuery(id+"F0.wireOp",EDGE,"E7.filletArc"),sQuery(id+"F2.wireOp",EDGE,"E11.0"),sQuery(id+"F2.wireOp",EDGE,"E13.1.8"),sQuery(id+"F2.wireOp",EDGE,"E13.1.9")])]}),makeQuery(id+"F5.opExtrude","SWEPT_FACE",FACE,{"disambiguationData":[OSD([sQuery(id+"F4.wireOp",EDGE,"E14")])]})]}),"instanceName":"11"});
            var Q14;
            Q14=makeQuery(id+"F6.opPattern","COPY",EDGE,{"derivedFrom":makeQuery(id+"F5.boolean.opBoolean","INTERSECT",EDGE,{"derivedFrom":[makeQuery(id+"F3.opLoft","SWEPT_FACE",FACE,{"disambiguationData":[OSD([sQuery(id+"F0.wireOp",EDGE,"E0"),sQuery(id+"F0.wireOp",EDGE,"E2"),sQuery(id+"F0.wireOp",EDGE,"E7.filletArc"),sQuery(id+"F2.wireOp",EDGE,"E11.0"),sQuery(id+"F2.wireOp",EDGE,"E13.1.8"),sQuery(id+"F2.wireOp",EDGE,"E13.1.9")])]}),makeQuery(id+"F5.opExtrude","SWEPT_FACE",FACE,{"disambiguationData":[OSD([sQuery(id+"F4.wireOp",EDGE,"E14")])]})]}),"instanceName":"12"});
            var Q15;
            Q15=makeQuery(id+"F6.opPattern","COPY",EDGE,{"derivedFrom":makeQuery(id+"F5.boolean.opBoolean","INTERSECT",EDGE,{"derivedFrom":[makeQuery(id+"F3.opLoft","SWEPT_FACE",FACE,{"disambiguationData":[OSD([sQuery(id+"F0.wireOp",EDGE,"E3"),sQuery(id+"F0.wireOp",EDGE,"E4.MirrorCS"),sQuery(id+"F0.wireOp",EDGE,"E10.filletArc"),sQuery(id+"F2.wireOp",EDGE,"E13.1.1"),sQuery(id+"F2.wireOp",EDGE,"E13.1.2"),sQuery(id+"F2.wireOp",EDGE,"E13.1.3")])]}),makeQuery(id+"F5.opExtrude","SWEPT_FACE",FACE,{"disambiguationData":[OSD([sQuery(id+"F4.wireOp",EDGE,"E14")])]})]}),"instanceName":"4"});
            var Q16;
            Q16=makeQuery(id+"F6.opPattern","COPY",EDGE,{"derivedFrom":makeQuery(id+"F5.boolean.opBoolean","INTERSECT",EDGE,{"derivedFrom":[makeQuery(id+"F3.opLoft","SWEPT_FACE",FACE,{"disambiguationData":[OSD([sQuery(id+"F0.wireOp",EDGE,"E3"),sQuery(id+"F0.wireOp",EDGE,"E4.MirrorCS"),sQuery(id+"F0.wireOp",EDGE,"E10.filletArc"),sQuery(id+"F2.wireOp",EDGE,"E13.1.1"),sQuery(id+"F2.wireOp",EDGE,"E13.1.2"),sQuery(id+"F2.wireOp",EDGE,"E13.1.3")])]}),makeQuery(id+"F5.opExtrude","SWEPT_FACE",FACE,{"disambiguationData":[OSD([sQuery(id+"F4.wireOp",EDGE,"E14")])]})]}),"instanceName":"3"});
            var Q17;
            Q17=makeQuery(id+"F6.opPattern","COPY",EDGE,{"derivedFrom":makeQuery(id+"F5.boolean.opBoolean","INTERSECT",EDGE,{"derivedFrom":[makeQuery(id+"F3.opLoft","SWEPT_FACE",FACE,{"disambiguationData":[OSD([sQuery(id+"F0.wireOp",EDGE,"E3"),sQuery(id+"F0.wireOp",EDGE,"E4.MirrorCS"),sQuery(id+"F0.wireOp",EDGE,"E10.filletArc"),sQuery(id+"F2.wireOp",EDGE,"E13.1.1"),sQuery(id+"F2.wireOp",EDGE,"E13.1.2"),sQuery(id+"F2.wireOp",EDGE,"E13.1.3")])]}),makeQuery(id+"F5.opExtrude","SWEPT_FACE",FACE,{"disambiguationData":[OSD([sQuery(id+"F4.wireOp",EDGE,"E14")])]})]}),"instanceName":"5"});
            var Q18;
            Q18=makeQuery(id+"F6.opPattern","COPY",EDGE,{"derivedFrom":makeQuery(id+"F5.boolean.opBoolean","INTERSECT",EDGE,{"derivedFrom":[makeQuery(id+"F3.opLoft","SWEPT_FACE",FACE,{"disambiguationData":[OSD([sQuery(id+"F0.wireOp",EDGE,"E3"),sQuery(id+"F0.wireOp",EDGE,"E4.MirrorCS"),sQuery(id+"F0.wireOp",EDGE,"E10.filletArc"),sQuery(id+"F2.wireOp",EDGE,"E13.1.1"),sQuery(id+"F2.wireOp",EDGE,"E13.1.2"),sQuery(id+"F2.wireOp",EDGE,"E13.1.3")])]}),makeQuery(id+"F5.opExtrude","SWEPT_FACE",FACE,{"disambiguationData":[OSD([sQuery(id+"F4.wireOp",EDGE,"E14")])]})]}),"instanceName":"6"});
            var Q19;
            Q19=makeQuery(id+"F6.opPattern","COPY",EDGE,{"derivedFrom":makeQuery(id+"F5.boolean.opBoolean","INTERSECT",EDGE,{"derivedFrom":[makeQuery(id+"F3.opLoft","SWEPT_FACE",FACE,{"disambiguationData":[OSD([sQuery(id+"F0.wireOp",EDGE,"E3"),sQuery(id+"F0.wireOp",EDGE,"E4.MirrorCS"),sQuery(id+"F0.wireOp",EDGE,"E10.filletArc"),sQuery(id+"F2.wireOp",EDGE,"E13.1.1"),sQuery(id+"F2.wireOp",EDGE,"E13.1.2"),sQuery(id+"F2.wireOp",EDGE,"E13.1.3")])]}),makeQuery(id+"F5.opExtrude","SWEPT_FACE",FACE,{"disambiguationData":[OSD([sQuery(id+"F4.wireOp",EDGE,"E14")])]})]}),"instanceName":"7"});
            var Q20;
            Q20=makeQuery(id+"F6.opPattern","COPY",EDGE,{"derivedFrom":makeQuery(id+"F5.boolean.opBoolean","INTERSECT",EDGE,{"derivedFrom":[makeQuery(id+"F3.opLoft","SWEPT_FACE",FACE,{"disambiguationData":[OSD([sQuery(id+"F0.wireOp",EDGE,"E3"),sQuery(id+"F0.wireOp",EDGE,"E4.MirrorCS"),sQuery(id+"F0.wireOp",EDGE,"E10.filletArc"),sQuery(id+"F2.wireOp",EDGE,"E13.1.1"),sQuery(id+"F2.wireOp",EDGE,"E13.1.2"),sQuery(id+"F2.wireOp",EDGE,"E13.1.3")])]}),makeQuery(id+"F5.opExtrude","SWEPT_FACE",FACE,{"disambiguationData":[OSD([sQuery(id+"F4.wireOp",EDGE,"E14")])]})]}),"instanceName":"8"});
            var Q21;
            Q21=makeQuery(id+"F6.opPattern","COPY",EDGE,{"derivedFrom":makeQuery(id+"F5.boolean.opBoolean","INTERSECT",EDGE,{"derivedFrom":[makeQuery(id+"F3.opLoft","SWEPT_FACE",FACE,{"disambiguationData":[OSD([sQuery(id+"F0.wireOp",EDGE,"E3"),sQuery(id+"F0.wireOp",EDGE,"E4.MirrorCS"),sQuery(id+"F0.wireOp",EDGE,"E10.filletArc"),sQuery(id+"F2.wireOp",EDGE,"E13.1.1"),sQuery(id+"F2.wireOp",EDGE,"E13.1.2"),sQuery(id+"F2.wireOp",EDGE,"E13.1.3")])]}),makeQuery(id+"F5.opExtrude","SWEPT_FACE",FACE,{"disambiguationData":[OSD([sQuery(id+"F4.wireOp",EDGE,"E14")])]})]}),"instanceName":"9"});
            var Q22;
            Q22=makeQuery(id+"F6.opPattern","COPY",EDGE,{"derivedFrom":makeQuery(id+"F5.boolean.opBoolean","INTERSECT",EDGE,{"derivedFrom":[makeQuery(id+"F3.opLoft","SWEPT_FACE",FACE,{"disambiguationData":[OSD([sQuery(id+"F0.wireOp",EDGE,"E3"),sQuery(id+"F0.wireOp",EDGE,"E4.MirrorCS"),sQuery(id+"F0.wireOp",EDGE,"E10.filletArc"),sQuery(id+"F2.wireOp",EDGE,"E13.1.1"),sQuery(id+"F2.wireOp",EDGE,"E13.1.2"),sQuery(id+"F2.wireOp",EDGE,"E13.1.3")])]}),makeQuery(id+"F5.opExtrude","SWEPT_FACE",FACE,{"disambiguationData":[OSD([sQuery(id+"F4.wireOp",EDGE,"E14")])]})]}),"instanceName":"10"});
            var Q23;
            Q23=makeQuery(id+"F6.opPattern","COPY",EDGE,{"derivedFrom":makeQuery(id+"F5.boolean.opBoolean","INTERSECT",EDGE,{"derivedFrom":[makeQuery(id+"F3.opLoft","SWEPT_FACE",FACE,{"disambiguationData":[OSD([sQuery(id+"F0.wireOp",EDGE,"E3"),sQuery(id+"F0.wireOp",EDGE,"E4.MirrorCS"),sQuery(id+"F0.wireOp",EDGE,"E10.filletArc"),sQuery(id+"F2.wireOp",EDGE,"E13.1.1"),sQuery(id+"F2.wireOp",EDGE,"E13.1.2"),sQuery(id+"F2.wireOp",EDGE,"E13.1.3")])]}),makeQuery(id+"F5.opExtrude","SWEPT_FACE",FACE,{"disambiguationData":[OSD([sQuery(id+"F4.wireOp",EDGE,"E14")])]})]}),"instanceName":"11"});
            var Q24;
            Q24=makeQuery(id+"F6.opPattern","COPY",EDGE,{"derivedFrom":makeQuery(id+"F5.boolean.opBoolean","INTERSECT",EDGE,{"derivedFrom":[makeQuery(id+"F3.opLoft","SWEPT_FACE",FACE,{"disambiguationData":[OSD([sQuery(id+"F0.wireOp",EDGE,"E3"),sQuery(id+"F0.wireOp",EDGE,"E4.MirrorCS"),sQuery(id+"F0.wireOp",EDGE,"E10.filletArc"),sQuery(id+"F2.wireOp",EDGE,"E13.1.1"),sQuery(id+"F2.wireOp",EDGE,"E13.1.2"),sQuery(id+"F2.wireOp",EDGE,"E13.1.3")])]}),makeQuery(id+"F5.opExtrude","SWEPT_FACE",FACE,{"disambiguationData":[OSD([sQuery(id+"F4.wireOp",EDGE,"E14")])]})]}),"instanceName":"12"});
            var Q25;
            Q25=makeQuery(id+"F6.opPattern","COPY",EDGE,{"derivedFrom":makeQuery(id+"F5.boolean.opBoolean","INTERSECT",EDGE,{"derivedFrom":[makeQuery(id+"F3.opLoft","SWEPT_FACE",FACE,{"disambiguationData":[OSD([sQuery(id+"F0.wireOp",EDGE,"E3"),sQuery(id+"F0.wireOp",EDGE,"E4.MirrorCS"),sQuery(id+"F0.wireOp",EDGE,"E10.filletArc"),sQuery(id+"F2.wireOp",EDGE,"E13.1.1"),sQuery(id+"F2.wireOp",EDGE,"E13.1.2"),sQuery(id+"F2.wireOp",EDGE,"E13.1.3")])]}),makeQuery(id+"F5.opExtrude","SWEPT_FACE",FACE,{"disambiguationData":[OSD([sQuery(id+"F4.wireOp",EDGE,"E14")])]})]}),"instanceName":"13"});
            var Q26;
            Q26=makeQuery(id+"F6.opPattern","COPY",EDGE,{"derivedFrom":makeQuery(id+"F5.boolean.opBoolean","INTERSECT",EDGE,{"derivedFrom":[makeQuery(id+"F3.opLoft","SWEPT_FACE",FACE,{"disambiguationData":[OSD([sQuery(id+"F0.wireOp",EDGE,"E3"),sQuery(id+"F0.wireOp",EDGE,"E4.MirrorCS"),sQuery(id+"F0.wireOp",EDGE,"E10.filletArc"),sQuery(id+"F2.wireOp",EDGE,"E13.1.1"),sQuery(id+"F2.wireOp",EDGE,"E13.1.2"),sQuery(id+"F2.wireOp",EDGE,"E13.1.3")])]}),makeQuery(id+"F5.opExtrude","SWEPT_FACE",FACE,{"disambiguationData":[OSD([sQuery(id+"F4.wireOp",EDGE,"E14")])]})]}),"instanceName":"14"});
            var Q27;
            Q27=makeQuery(id+"F5.boolean.opBoolean","INTERSECT",EDGE,{"derivedFrom":[makeQuery(id+"F3.opLoft","SWEPT_FACE",FACE,{"disambiguationData":[OSD([sQuery(id+"F0.wireOp",EDGE,"E3"),sQuery(id+"F0.wireOp",EDGE,"E4.MirrorCS"),sQuery(id+"F0.wireOp",EDGE,"E10.filletArc"),sQuery(id+"F2.wireOp",EDGE,"E13.1.1"),sQuery(id+"F2.wireOp",EDGE,"E13.1.2"),sQuery(id+"F2.wireOp",EDGE,"E13.1.3")])]}),makeQuery(id+"F5.opExtrude","SWEPT_FACE",FACE,{"disambiguationData":[OSD([sQuery(id+"F4.wireOp",EDGE,"E14")])]})]});
            var Q28;
            Q28=makeQuery(id+"F6.opPattern","COPY",EDGE,{"derivedFrom":makeQuery(id+"F5.boolean.opBoolean","INTERSECT",EDGE,{"derivedFrom":[makeQuery(id+"F3.opLoft","SWEPT_FACE",FACE,{"disambiguationData":[OSD([sQuery(id+"F0.wireOp",EDGE,"E3"),sQuery(id+"F0.wireOp",EDGE,"E4.MirrorCS"),sQuery(id+"F0.wireOp",EDGE,"E10.filletArc"),sQuery(id+"F2.wireOp",EDGE,"E13.1.1"),sQuery(id+"F2.wireOp",EDGE,"E13.1.2"),sQuery(id+"F2.wireOp",EDGE,"E13.1.3")])]}),makeQuery(id+"F5.opExtrude","SWEPT_FACE",FACE,{"disambiguationData":[OSD([sQuery(id+"F4.wireOp",EDGE,"E14")])]})]}),"instanceName":"1"});
            var Q29;
            Q29=makeQuery(id+"F6.opPattern","COPY",EDGE,{"derivedFrom":makeQuery(id+"F5.boolean.opBoolean","INTERSECT",EDGE,{"derivedFrom":[makeQuery(id+"F3.opLoft","SWEPT_FACE",FACE,{"disambiguationData":[OSD([sQuery(id+"F0.wireOp",EDGE,"E3"),sQuery(id+"F0.wireOp",EDGE,"E4.MirrorCS"),sQuery(id+"F0.wireOp",EDGE,"E10.filletArc"),sQuery(id+"F2.wireOp",EDGE,"E13.1.1"),sQuery(id+"F2.wireOp",EDGE,"E13.1.2"),sQuery(id+"F2.wireOp",EDGE,"E13.1.3")])]}),makeQuery(id+"F5.opExtrude","SWEPT_FACE",FACE,{"disambiguationData":[OSD([sQuery(id+"F4.wireOp",EDGE,"E14")])]})]}),"instanceName":"2"});
            fillet(context, id + "F7", {"entities" : qUnion([Q0, Q1, Q2, Q3, Q4, Q5, Q6, Q7, Q8, Q9, Q10, Q11, Q12, Q13, Q14, Q15, Q16, Q17, Q18, Q19, Q20, Q21, Q22, Q23, Q24, Q25, Q26, Q27, Q28, Q29]), "radius" : 1.6 * mm, "tangentPropagation" : true, "allowEdgeOverflow" : false});
        }
        {
            var Q0;
            {var subQ0=sQuery(id+"F2.wireOp",EDGE,"E13.1.0");Q0=makeQuery(id+"F6.opPattern","COPY",BODY,{"derivedFrom":makeQuery(id+"F3.opLoft","SWEPT_BODY",BODY,{"disambiguationData":[OSD([makeQuery(id+"F0.imprint","IMPRINT",FACE,{"disambiguationData":[TD([[makeQuery(id+"F0.imprint","IMPRINT",EDGE,{"derivedFrom":sQuery(id+"F0.wireOp",EDGE,"E1.trimOffspring")}),1.0]])]}),makeQuery(id+"F2.imprint","IMPRINT",FACE,{"disambiguationData":[TD([[makeQuery(id+"F2.imprint","IMPRINT",EDGE,{"derivedFrom":subQ0}),1.0]])]})])]}),"instanceName":"14"});}
            var Q1;
            {var subQ0=sQuery(id+"F2.wireOp",EDGE,"E13.1.0");Q1=makeQuery(id+"F6.opPattern","COPY",BODY,{"derivedFrom":makeQuery(id+"F3.opLoft","SWEPT_BODY",BODY,{"disambiguationData":[OSD([makeQuery(id+"F0.imprint","IMPRINT",FACE,{"disambiguationData":[TD([[makeQuery(id+"F0.imprint","IMPRINT",EDGE,{"derivedFrom":sQuery(id+"F0.wireOp",EDGE,"E1.trimOffspring")}),1.0]])]}),makeQuery(id+"F2.imprint","IMPRINT",FACE,{"disambiguationData":[TD([[makeQuery(id+"F2.imprint","IMPRINT",EDGE,{"derivedFrom":subQ0}),1.0]])]})])]}),"instanceName":"13"});}
            var Q2;
            {var subQ0=sQuery(id+"F2.wireOp",EDGE,"E13.1.0");Q2=makeQuery(id+"F6.opPattern","COPY",BODY,{"derivedFrom":makeQuery(id+"F3.opLoft","SWEPT_BODY",BODY,{"disambiguationData":[OSD([makeQuery(id+"F0.imprint","IMPRINT",FACE,{"disambiguationData":[TD([[makeQuery(id+"F0.imprint","IMPRINT",EDGE,{"derivedFrom":sQuery(id+"F0.wireOp",EDGE,"E1.trimOffspring")}),1.0]])]}),makeQuery(id+"F2.imprint","IMPRINT",FACE,{"disambiguationData":[TD([[makeQuery(id+"F2.imprint","IMPRINT",EDGE,{"derivedFrom":subQ0}),1.0]])]})])]}),"instanceName":"12"});}
            var Q3;
            {var subQ0=sQuery(id+"F2.wireOp",EDGE,"E13.1.0");Q3=makeQuery(id+"F6.opPattern","COPY",BODY,{"derivedFrom":makeQuery(id+"F3.opLoft","SWEPT_BODY",BODY,{"disambiguationData":[OSD([makeQuery(id+"F0.imprint","IMPRINT",FACE,{"disambiguationData":[TD([[makeQuery(id+"F0.imprint","IMPRINT",EDGE,{"derivedFrom":sQuery(id+"F0.wireOp",EDGE,"E1.trimOffspring")}),1.0]])]}),makeQuery(id+"F2.imprint","IMPRINT",FACE,{"disambiguationData":[TD([[makeQuery(id+"F2.imprint","IMPRINT",EDGE,{"derivedFrom":subQ0}),1.0]])]})])]}),"instanceName":"11"});}
            var Q4;
            {var subQ0=sQuery(id+"F2.wireOp",EDGE,"E13.1.0");Q4=makeQuery(id+"F6.opPattern","COPY",BODY,{"derivedFrom":makeQuery(id+"F3.opLoft","SWEPT_BODY",BODY,{"disambiguationData":[OSD([makeQuery(id+"F0.imprint","IMPRINT",FACE,{"disambiguationData":[TD([[makeQuery(id+"F0.imprint","IMPRINT",EDGE,{"derivedFrom":sQuery(id+"F0.wireOp",EDGE,"E1.trimOffspring")}),1.0]])]}),makeQuery(id+"F2.imprint","IMPRINT",FACE,{"disambiguationData":[TD([[makeQuery(id+"F2.imprint","IMPRINT",EDGE,{"derivedFrom":subQ0}),1.0]])]})])]}),"instanceName":"10"});}
            var Q5;
            {var subQ0=sQuery(id+"F2.wireOp",EDGE,"E13.1.0");Q5=makeQuery(id+"F6.opPattern","COPY",BODY,{"derivedFrom":makeQuery(id+"F3.opLoft","SWEPT_BODY",BODY,{"disambiguationData":[OSD([makeQuery(id+"F0.imprint","IMPRINT",FACE,{"disambiguationData":[TD([[makeQuery(id+"F0.imprint","IMPRINT",EDGE,{"derivedFrom":sQuery(id+"F0.wireOp",EDGE,"E1.trimOffspring")}),1.0]])]}),makeQuery(id+"F2.imprint","IMPRINT",FACE,{"disambiguationData":[TD([[makeQuery(id+"F2.imprint","IMPRINT",EDGE,{"derivedFrom":subQ0}),1.0]])]})])]}),"instanceName":"9"});}
            var Q6;
            {var subQ0=sQuery(id+"F2.wireOp",EDGE,"E13.1.0");Q6=makeQuery(id+"F6.opPattern","COPY",BODY,{"derivedFrom":makeQuery(id+"F3.opLoft","SWEPT_BODY",BODY,{"disambiguationData":[OSD([makeQuery(id+"F0.imprint","IMPRINT",FACE,{"disambiguationData":[TD([[makeQuery(id+"F0.imprint","IMPRINT",EDGE,{"derivedFrom":sQuery(id+"F0.wireOp",EDGE,"E1.trimOffspring")}),1.0]])]}),makeQuery(id+"F2.imprint","IMPRINT",FACE,{"disambiguationData":[TD([[makeQuery(id+"F2.imprint","IMPRINT",EDGE,{"derivedFrom":subQ0}),1.0]])]})])]}),"instanceName":"5"});}
            var Q7;
            {var subQ0=sQuery(id+"F2.wireOp",EDGE,"E13.1.0");Q7=makeQuery(id+"F6.opPattern","COPY",BODY,{"derivedFrom":makeQuery(id+"F3.opLoft","SWEPT_BODY",BODY,{"disambiguationData":[OSD([makeQuery(id+"F0.imprint","IMPRINT",FACE,{"disambiguationData":[TD([[makeQuery(id+"F0.imprint","IMPRINT",EDGE,{"derivedFrom":sQuery(id+"F0.wireOp",EDGE,"E1.trimOffspring")}),1.0]])]}),makeQuery(id+"F2.imprint","IMPRINT",FACE,{"disambiguationData":[TD([[makeQuery(id+"F2.imprint","IMPRINT",EDGE,{"derivedFrom":subQ0}),1.0]])]})])]}),"instanceName":"4"});}
            var Q8;
            {var subQ0=sQuery(id+"F2.wireOp",EDGE,"E13.1.0");Q8=makeQuery(id+"F6.opPattern","COPY",BODY,{"derivedFrom":makeQuery(id+"F3.opLoft","SWEPT_BODY",BODY,{"disambiguationData":[OSD([makeQuery(id+"F0.imprint","IMPRINT",FACE,{"disambiguationData":[TD([[makeQuery(id+"F0.imprint","IMPRINT",EDGE,{"derivedFrom":sQuery(id+"F0.wireOp",EDGE,"E1.trimOffspring")}),1.0]])]}),makeQuery(id+"F2.imprint","IMPRINT",FACE,{"disambiguationData":[TD([[makeQuery(id+"F2.imprint","IMPRINT",EDGE,{"derivedFrom":subQ0}),1.0]])]})])]}),"instanceName":"3"});}
            var Q9;
            {var subQ0=sQuery(id+"F2.wireOp",EDGE,"E13.1.0");Q9=makeQuery(id+"F6.opPattern","COPY",BODY,{"derivedFrom":makeQuery(id+"F3.opLoft","SWEPT_BODY",BODY,{"disambiguationData":[OSD([makeQuery(id+"F0.imprint","IMPRINT",FACE,{"disambiguationData":[TD([[makeQuery(id+"F0.imprint","IMPRINT",EDGE,{"derivedFrom":sQuery(id+"F0.wireOp",EDGE,"E1.trimOffspring")}),1.0]])]}),makeQuery(id+"F2.imprint","IMPRINT",FACE,{"disambiguationData":[TD([[makeQuery(id+"F2.imprint","IMPRINT",EDGE,{"derivedFrom":subQ0}),1.0]])]})])]}),"instanceName":"2"});}
            var Q10;
            {var subQ0=sQuery(id+"F2.wireOp",EDGE,"E13.1.0");Q10=makeQuery(id+"F6.opPattern","COPY",BODY,{"derivedFrom":makeQuery(id+"F3.opLoft","SWEPT_BODY",BODY,{"disambiguationData":[OSD([makeQuery(id+"F0.imprint","IMPRINT",FACE,{"disambiguationData":[TD([[makeQuery(id+"F0.imprint","IMPRINT",EDGE,{"derivedFrom":sQuery(id+"F0.wireOp",EDGE,"E1.trimOffspring")}),1.0]])]}),makeQuery(id+"F2.imprint","IMPRINT",FACE,{"disambiguationData":[TD([[makeQuery(id+"F2.imprint","IMPRINT",EDGE,{"derivedFrom":subQ0}),1.0]])]})])]}),"instanceName":"1"});}
            var Q11;
            {var subQ0=sQuery(id+"F2.wireOp",EDGE,"E13.1.0");Q11=makeQuery(id+"F3.opLoft","SWEPT_BODY",BODY,{"disambiguationData":[OSD([makeQuery(id+"F0.imprint","IMPRINT",FACE,{"disambiguationData":[TD([[makeQuery(id+"F0.imprint","IMPRINT",EDGE,{"derivedFrom":sQuery(id+"F0.wireOp",EDGE,"E1.trimOffspring")}),1.0]])]}),makeQuery(id+"F2.imprint","IMPRINT",FACE,{"disambiguationData":[TD([[makeQuery(id+"F2.imprint","IMPRINT",EDGE,{"derivedFrom":subQ0}),1.0]])]})])]});}
            var Q12;
            {var subQ0=sQuery(id+"F2.wireOp",EDGE,"E13.1.0");Q12=makeQuery(id+"F6.opPattern","COPY",BODY,{"derivedFrom":makeQuery(id+"F3.opLoft","SWEPT_BODY",BODY,{"disambiguationData":[OSD([makeQuery(id+"F0.imprint","IMPRINT",FACE,{"disambiguationData":[TD([[makeQuery(id+"F0.imprint","IMPRINT",EDGE,{"derivedFrom":sQuery(id+"F0.wireOp",EDGE,"E1.trimOffspring")}),1.0]])]}),makeQuery(id+"F2.imprint","IMPRINT",FACE,{"disambiguationData":[TD([[makeQuery(id+"F2.imprint","IMPRINT",EDGE,{"derivedFrom":subQ0}),1.0]])]})])]}),"instanceName":"6"});}
            var Q13;
            {var subQ0=sQuery(id+"F2.wireOp",EDGE,"E13.1.0");Q13=makeQuery(id+"F6.opPattern","COPY",BODY,{"derivedFrom":makeQuery(id+"F3.opLoft","SWEPT_BODY",BODY,{"disambiguationData":[OSD([makeQuery(id+"F0.imprint","IMPRINT",FACE,{"disambiguationData":[TD([[makeQuery(id+"F0.imprint","IMPRINT",EDGE,{"derivedFrom":sQuery(id+"F0.wireOp",EDGE,"E1.trimOffspring")}),1.0]])]}),makeQuery(id+"F2.imprint","IMPRINT",FACE,{"disambiguationData":[TD([[makeQuery(id+"F2.imprint","IMPRINT",EDGE,{"derivedFrom":subQ0}),1.0]])]})])]}),"instanceName":"7"});}
            var Q14;
            {var subQ0=sQuery(id+"F2.wireOp",EDGE,"E13.1.0");Q14=makeQuery(id+"F6.opPattern","COPY",BODY,{"derivedFrom":makeQuery(id+"F3.opLoft","SWEPT_BODY",BODY,{"disambiguationData":[OSD([makeQuery(id+"F0.imprint","IMPRINT",FACE,{"disambiguationData":[TD([[makeQuery(id+"F0.imprint","IMPRINT",EDGE,{"derivedFrom":sQuery(id+"F0.wireOp",EDGE,"E1.trimOffspring")}),1.0]])]}),makeQuery(id+"F2.imprint","IMPRINT",FACE,{"disambiguationData":[TD([[makeQuery(id+"F2.imprint","IMPRINT",EDGE,{"derivedFrom":subQ0}),1.0]])]})])]}),"instanceName":"8"});}
            booleanBodies(context, id + "F8", {"operationType" : BooleanOperationType.UNION, "tools" : qUnion([Q0, Q1, Q2, Q3, Q4, Q5, Q6, Q7, Q8, Q9, Q10, Q11, Q12, Q13, Q14])});
        }
        {
            var Q0;
            {var subQ0=sQuery(id+"F2.wireOp",EDGE,"E13.1.0");var subQ3=makeQuery(id+"F5.boolean.opBoolean","MERGE",FACE,{"derivedFrom":[makeQuery(id+"F3.opLoft","CAP_FACE",FACE,{"disambiguationData":[OSD([makeQuery(id+"F2.imprint","IMPRINT",FACE,{"disambiguationData":[TD([[makeQuery(id+"F2.imprint","IMPRINT",EDGE,{"derivedFrom":subQ0}),1.0]])]})])],"isStart":true}),makeQuery(id+"F5.opExtrude","CAP_FACE",FACE,{"disambiguationData":[OSD([sQuery(id+"F4.wireOp",EDGE,"E14")])],"isStart":true})]});Q0=makeQuery(id+"F8.opBoolean","MERGE",FACE,{"derivedFrom":[subQ3,makeQuery(id+"F6.opPattern","COPY",FACE,{"derivedFrom":subQ3,"instanceName":"1"}),makeQuery(id+"F6.opPattern","COPY",FACE,{"derivedFrom":subQ3,"instanceName":"2"}),makeQuery(id+"F6.opPattern","COPY",FACE,{"derivedFrom":subQ3,"instanceName":"3"}),makeQuery(id+"F6.opPattern","COPY",FACE,{"derivedFrom":subQ3,"instanceName":"4"}),makeQuery(id+"F6.opPattern","COPY",FACE,{"derivedFrom":subQ3,"instanceName":"5"}),makeQuery(id+"F6.opPattern","COPY",FACE,{"derivedFrom":subQ3,"instanceName":"6"}),makeQuery(id+"F6.opPattern","COPY",FACE,{"derivedFrom":subQ3,"instanceName":"7"}),makeQuery(id+"F6.opPattern","COPY",FACE,{"derivedFrom":subQ3,"instanceName":"8"}),makeQuery(id+"F6.opPattern","COPY",FACE,{"derivedFrom":subQ3,"instanceName":"9"}),makeQuery(id+"F6.opPattern","COPY",FACE,{"derivedFrom":subQ3,"instanceName":"10"}),makeQuery(id+"F6.opPattern","COPY",FACE,{"derivedFrom":subQ3,"instanceName":"11"}),makeQuery(id+"F6.opPattern","COPY",FACE,{"derivedFrom":subQ3,"instanceName":"12"}),makeQuery(id+"F6.opPattern","COPY",FACE,{"derivedFrom":subQ3,"instanceName":"13"}),makeQuery(id+"F6.opPattern","COPY",FACE,{"derivedFrom":subQ3,"instanceName":"14"})]});}
            var sketch = newSketch(context, id + "F9", { "sketchPlane" : qUnion([Q0])});
            skCircle(sketch, "E15", {"center": v(0, 0) * mm, "radius": 6.35 * mm});
            skSolve(sketch);
        }
        {
            var Q0;
            Q0 = qSketchRegion(id + "F9", true);
            extrude(context, id + "F10", {"entities" : qUnion([Q0]), "operationType" : NewBodyOperationType.REMOVE, "endBound" : BoundingType.THROUGH_ALL, "oppositeDirection" : true, "depth" : 25.4 * mm});
        }
    });
